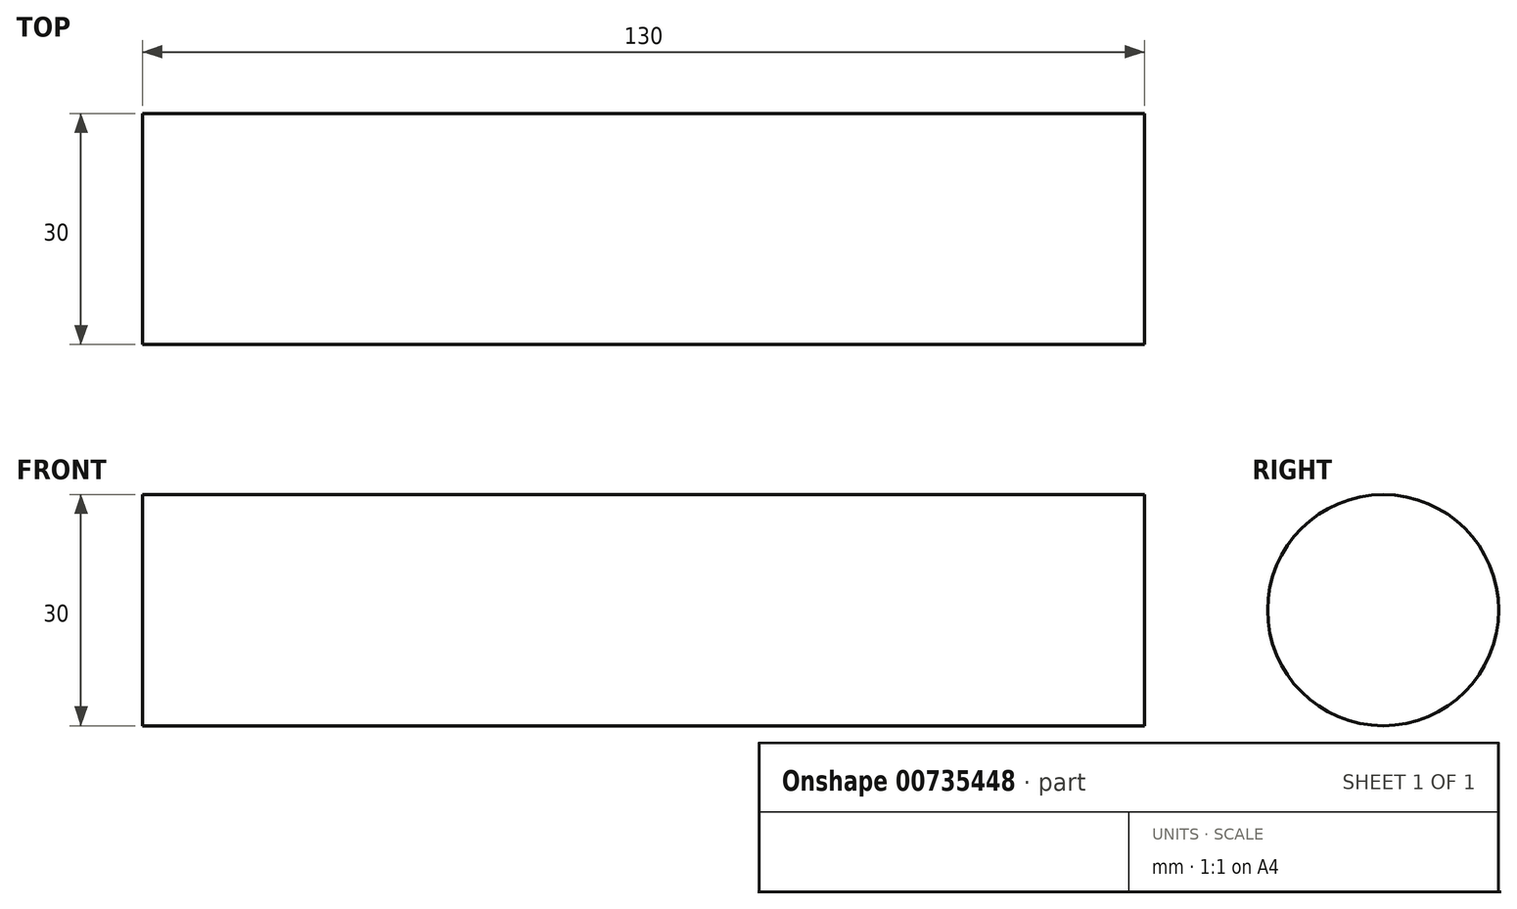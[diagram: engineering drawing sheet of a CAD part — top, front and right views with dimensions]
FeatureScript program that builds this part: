
annotation { "Feature Type Name" : "Feature", "Feature Type Description" : "" }
export const myFeature = defineFeature(function(context is Context, id is Id, definition is map)
    precondition{}
    {
        {
            var Q0;
            Q0=qCreatedBy(makeId("Top.planeOp"),FACE);
            var sketch = newSketch(context, id + "F0", { "sketchPlane" : qUnion([Q0])});
            skLineSegment(sketch, "E0", {"start": v(0, 0) * mm, "end": v(0, 15) * mm});
            skLineSegment(sketch, "E1", {"start": v(0, 15) * mm, "end": v(-130, 15) * mm});
            skLineSegment(sketch, "E2", {"start": v(0, 0) * mm, "end": v(-130, 0) * mm});
            skLineSegment(sketch, "E3", {"start": v(-130, 0) * mm, "end": v(-130, 15) * mm});
            skLineSegment(sketch, "E4", {"start": v(-130, 0) * mm, "end": v(-130, -15) * mm});
            skLineSegment(sketch, "E5", {"start": v(-130, -15) * mm, "end": v(0, -15) * mm});
            skLineSegment(sketch, "E6", {"start": v(0, -15) * mm, "end": v(0, 0) * mm});
            skSolve(sketch);
        }
        {
            var Q0;
            Q0=makeQuery(id+"F0.imprint","IMPRINT",FACE,{"disambiguationData":[TD([[makeQuery(id+"F0.imprint","IMPRINT",EDGE,{"derivedFrom":sQuery(id+"F0.wireOp",EDGE,"E0")}),1.0]])]});
            var Q1;
            Q1=sQuery(id+"F0.wireOp",EDGE,"E2");
            revolve(context, id + "F1", {"surfaceOperationType" : NewSurfaceOperationType.NEW, "entities" : qUnion([Q0]), "axis" : qUnion([Q1]), "revolveType" : RevolveType.FULL});
        }
    });
